# Revit family: ADB Armoire Gril Gaz 610_620
name_source: partatom
category: Equipement spécialisé
units: mm (PartAtom-declared; Revit-internal decimal feet)

## family parameters
Basée sur le plan de construction = Non
Conserver l'orientation des annotations = Non
Cote de connecteur circulaire = Utiliser le diamètre
Couper avec des vides une fois chargée = Non
Numéro OmniClass = 23.40.40.14.17.11
Partagée = Non
Repère de localisation dans la pièce = Non
Titre OmniClass = Cookers, Ovens, Stoves
Toujours verticalement = Oui
Type d'élément = Normal

## types (7) — shared parameters
C = 300 mm  [stored 0.984252 ft]
Commentaires du type = Gamme Ambassade - Grils et planchas gaz
Diamètre de Raccordement Gaz = 20.96 mm
F = 810 mm
Fabricant = Société Industrielle de Lacanche
URL = https://www.ambassade-de-bourgogne.com
URL catalogue = https://www.ambassade-de-bourgogne.com
zero-valued in all types: Elévation par défaut

## per-type parameters (varying)
| type | Bac | CKG | D | Description | E | Position bouton | Position interrupteur | Puissance Gaz kW | Table |
| CMG 610 SRKC | Oui | Non | 795 mm  [stored 2.60827 ft] | Gril chrome nervuré gaz | 45 mm  [stored 0.147638 ft] | 203 mm  [stored 0.66601 ft] | 790 mm  [stored 2.59186 ft] | 8.5 | CME_CMG 610 SLK_SLKC_SRK_SRKC_SLR_SLRC : SRKC |
| CMG 610 SRK | Oui | Non | 795 mm  [stored 2.60827 ft] | Gril acier nervuré gaz | 45 mm  [stored 0.147638 ft] | 203 mm  [stored 0.66601 ft] | 790 mm  [stored 2.59186 ft] | 8.5 | CME_CMG 610 SLK_SLKC_SRK_SRKC_SLR_SLRC : SRK |
| CMG 610 SLK | Oui | Non | 795 mm  [stored 2.60827 ft] | Gril acier lisse gaz | 45 mm  [stored 0.147638 ft] | 203 mm  [stored 0.66601 ft] | 790 mm  [stored 2.59186 ft] | 8.5 | CME_CMG 610 SLK_SLKC_SRK_SRKC_SLR_SLRC : SLK |
| CMG 610 SLKC | Oui | Non | 795 mm  [stored 2.60827 ft] | Gril chrome lisse gaz | 45 mm  [stored 0.147638 ft] | 203 mm  [stored 0.66601 ft] | 790 mm  [stored 2.59186 ft] | 8.5 | CME_CMG 610 SLK_SLKC_SRK_SRKC_SLR_SLRC : SLKC |
| CMG 620 CKG | Non | Oui | 740 mm  [stored 2.42782 ft] | Gril Gaz à pierre de lave | 40 mm  [stored 0.131234 ft] | 90 mm  [stored 0.295276 ft] | 805 mm | 12 | CMG620 CKG_gril gaz : CKG |
| CMG 610 SLR | Oui | Non | 795 mm  [stored 2.60827 ft] | Gril acier lisse 1/2 nervuré gaz | 45 mm  [stored 0.147638 ft] | 203 mm  [stored 0.66601 ft] | 790 mm  [stored 2.59186 ft] | 8.5 | CME_CMG 610 SLK_SLKC_SRK_SRKC_SLR_SLRC : SLR |
| CMG 610 SLRC | Oui | Non | 795 mm  [stored 2.60827 ft] | Gril chrome lisse 1/2 nervuré gaz | 45 mm  [stored 0.147638 ft] | 203 mm  [stored 0.66601 ft] | 790 mm  [stored 2.59186 ft] | 8.5 | CME_CMG 610 SLK_SLKC_SRK_SRKC_SLR_SLRC : SLRC |

note: column(s) folded — value = type name in every type: Modèle

note: [stored X ft] marks values corroborated as IEEE doubles in the binary element streams (Revit-internal decimal feet)
